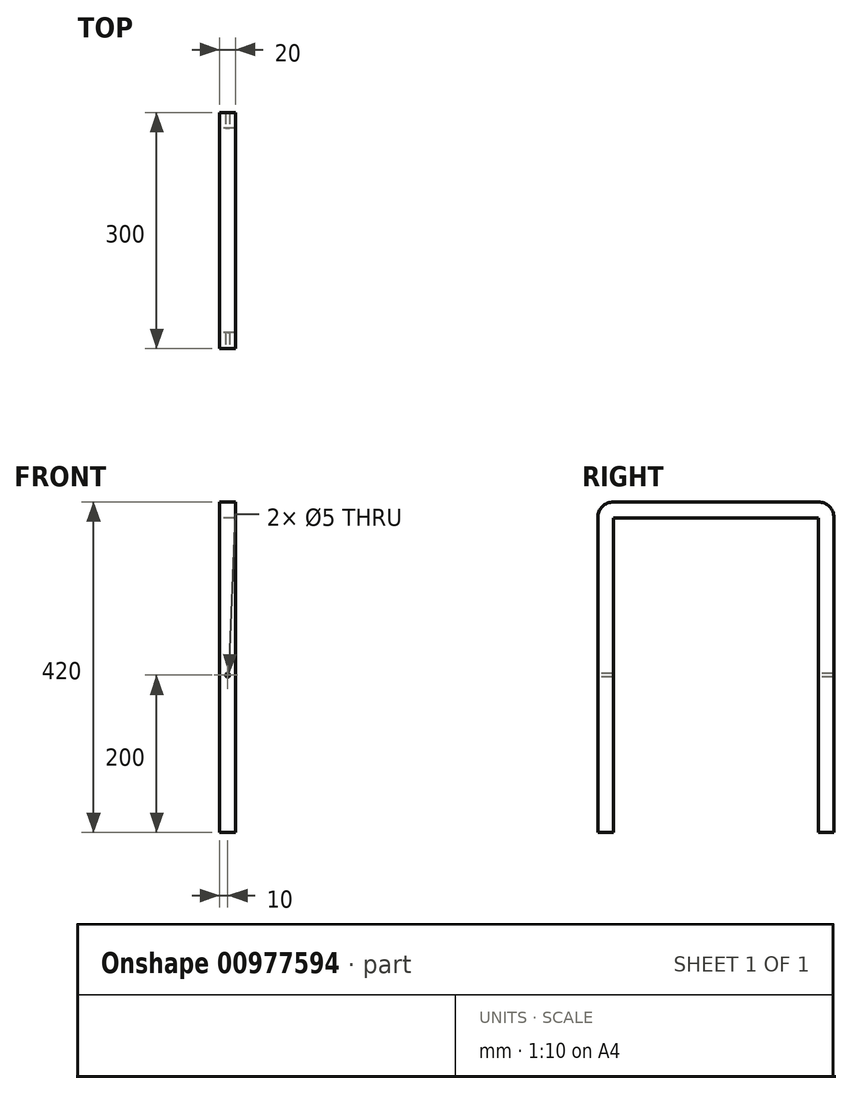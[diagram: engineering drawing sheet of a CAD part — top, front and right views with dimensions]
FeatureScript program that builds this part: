
annotation { "Feature Type Name" : "Feature", "Feature Type Description" : "" }
export const myFeature = defineFeature(function(context is Context, id is Id, definition is map)
    precondition{}
    {
        {
            var Q0;
            Q0=qCreatedBy(makeId("Right.planeOp"),FACE);
            var sketch = newSketch(context, id + "F0", { "sketchPlane" : qUnion([Q0])});
            skLineSegment(sketch, "E0.bottom", {"start": v(-150, 200) * mm, "end": v(-130, 200) * mm});
            skLineSegment(sketch, "E0.top", {"start": v(-150, -200) * mm, "end": v(-130, -200) * mm});
            skLineSegment(sketch, "E0.left", {"start": v(-150, 200) * mm, "end": v(-150, -200) * mm});
            skLineSegment(sketch, "E0.right", {"start": v(-130, 200) * mm, "end": v(-130, -200) * mm});
            skPoint(sketch, "E0.middle", {"position": v(-140, 0) * mm});
            skLineSegment(sketch, "E1.bottom", {"start": v(130, 200) * mm, "end": v(150, 200) * mm});
            skLineSegment(sketch, "E1.top", {"start": v(130, -200) * mm, "end": v(150, -200) * mm});
            skLineSegment(sketch, "E1.left", {"start": v(130, 200) * mm, "end": v(130, -200) * mm});
            skLineSegment(sketch, "E1.right", {"start": v(150, 200) * mm, "end": v(150, -200) * mm});
            skPoint(sketch, "E1.middle", {"position": v(140, 0) * mm});
            skLineSegment(sketch, "E2.bottom", {"start": v(130, 200) * mm, "end": v(-130, 200) * mm});
            skLineSegment(sketch, "E2.top", {"start": v(130, 220) * mm, "end": v(-130, 220) * mm});
            skLineSegment(sketch, "E2.left", {"start": v(130, 200) * mm, "end": v(130, 220) * mm});
            skLineSegment(sketch, "E2.right", {"start": v(-130, 200) * mm, "end": v(-130, 220) * mm});
            skPoint(sketch, "E2.middle", {"position": v(0, 210) * mm});
            skArc(sketch, "E3", {"start": v(-150, 200) * mm, "mid": v(-144.14, 214.14) * mm, "end": v(-130, 220) * mm});
            skArc(sketch, "E4", {"start": v(150, 200) * mm, "mid": v(144.14, 214.14) * mm, "end": v(130, 220) * mm});
            skSolve(sketch);
        }
        {
            var Q0;
            Q0=makeQuery(id+"F0.imprint","IMPRINT",FACE,{"disambiguationData":[TD([[makeQuery(id+"F0.imprint","IMPRINT",EDGE,{"derivedFrom":sQuery(id+"F0.wireOp",EDGE,"E0.bottom")}),-1.0]])]});
            var Q1;
            Q1=makeQuery(id+"F0.imprint","IMPRINT",FACE,{"disambiguationData":[TD([[makeQuery(id+"F0.imprint","IMPRINT",EDGE,{"derivedFrom":sQuery(id+"F0.wireOp",EDGE,"E0.bottom")}),1.0]])]});
            var Q2;
            Q2=makeQuery(id+"F0.imprint","IMPRINT",FACE,{"disambiguationData":[TD([[makeQuery(id+"F0.imprint","IMPRINT",EDGE,{"derivedFrom":sQuery(id+"F0.wireOp",EDGE,"E2.bottom")}),-1.0]])]});
            var Q3;
            Q3=makeQuery(id+"F0.imprint","IMPRINT",FACE,{"disambiguationData":[TD([[makeQuery(id+"F0.imprint","IMPRINT",EDGE,{"derivedFrom":sQuery(id+"F0.wireOp",EDGE,"E1.bottom")}),1.0]])]});
            var Q4;
            Q4=makeQuery(id+"F0.imprint","IMPRINT",FACE,{"disambiguationData":[TD([[makeQuery(id+"F0.imprint","IMPRINT",EDGE,{"derivedFrom":sQuery(id+"F0.wireOp",EDGE,"E1.bottom")}),-1.0]])]});
            extrude(context, id + "F1", {"entities" : qUnion([Q0, Q1, Q2, Q3, Q4]), "endBound" : BoundingType.SYMMETRIC, "depth" : 20 * mm, "offsetDistance" : 25 * mm});
        }
        {
            var Q0;
            Q0=makeQuery(id+"F1.opExtrude","SWEPT_FACE",FACE,{"disambiguationData":[OSD([sQuery(id+"F0.wireOp",EDGE,"E0.left")])]});
            var sketch = newSketch(context, id + "F2", { "sketchPlane" : qUnion([Q0])});
            skCircle(sketch, "E5", {"center": v(0, 0) * mm, "radius": 2.5 * mm});
            skSolve(sketch);
        }
        {
            var Q0;
            Q0 = qSketchRegion(id + "F2", true);
            extrude(context, id + "F3", {"entities" : qUnion([Q0]), "operationType" : NewBodyOperationType.REMOVE, "oppositeDirection" : true, "depth" : 3000 * mm, "offsetDistance" : 25 * mm});
        }
    });
